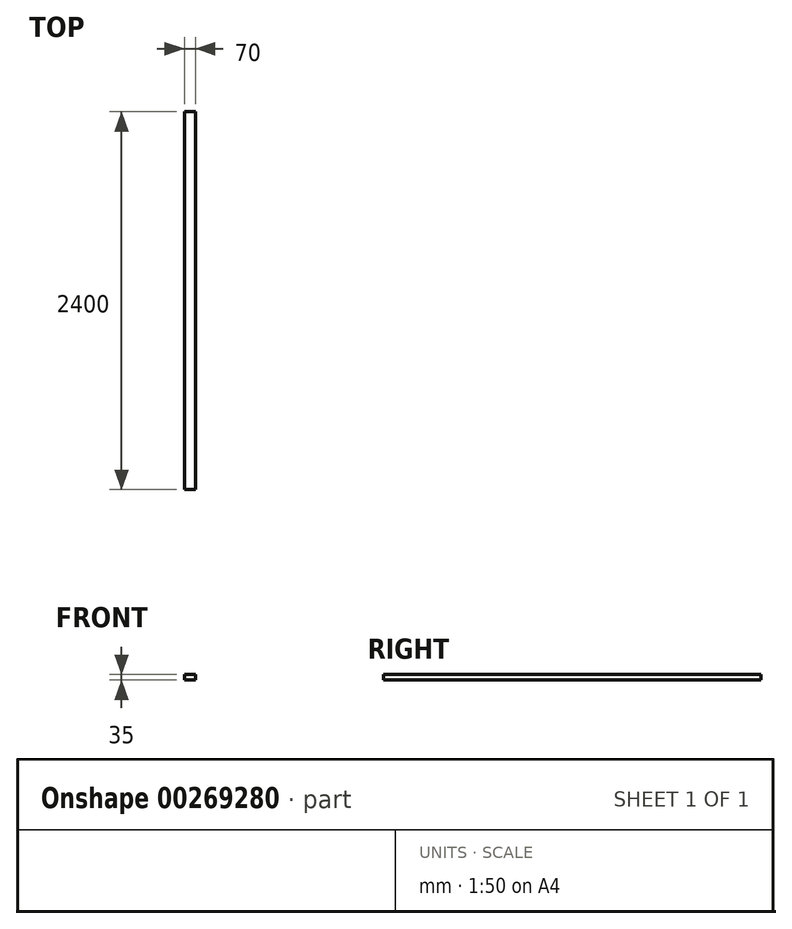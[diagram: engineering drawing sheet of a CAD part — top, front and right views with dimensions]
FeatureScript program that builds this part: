
annotation { "Feature Type Name" : "Feature", "Feature Type Description" : "" }
export const myFeature = defineFeature(function(context is Context, id is Id, definition is map)
    precondition{}
    {
        {
            var Q0;
            Q0=qCreatedBy(makeId("Front.planeOp"),FACE);
            var sketch = newSketch(context, id + "F0", { "sketchPlane" : qUnion([Q0])});
            skLineSegment(sketch, "E0.bottom", {"start": v(-35, 17.26) * mm, "end": v(35, 17.26) * mm});
            skLineSegment(sketch, "E0.top", {"start": v(-35, -17.74) * mm, "end": v(35, -17.74) * mm});
            skLineSegment(sketch, "E0.left", {"start": v(-35, 17.26) * mm, "end": v(-35, -17.74) * mm});
            skLineSegment(sketch, "E0.right", {"start": v(35, 17.26) * mm, "end": v(35, -17.74) * mm});
            skSolve(sketch);
        }
        {
            assignVariable(context, id + "F1", {"name" : "Length", "anyValue" : 2400});
        }
        {
            var Q0;
            Q0=qSketchRegion(id+"F0",true);
            extrude(context, id + "F2", {"entities" : qUnion([Q0]), "depth" : (getVariable(context, 'Length')) * mm});
        }
    });
